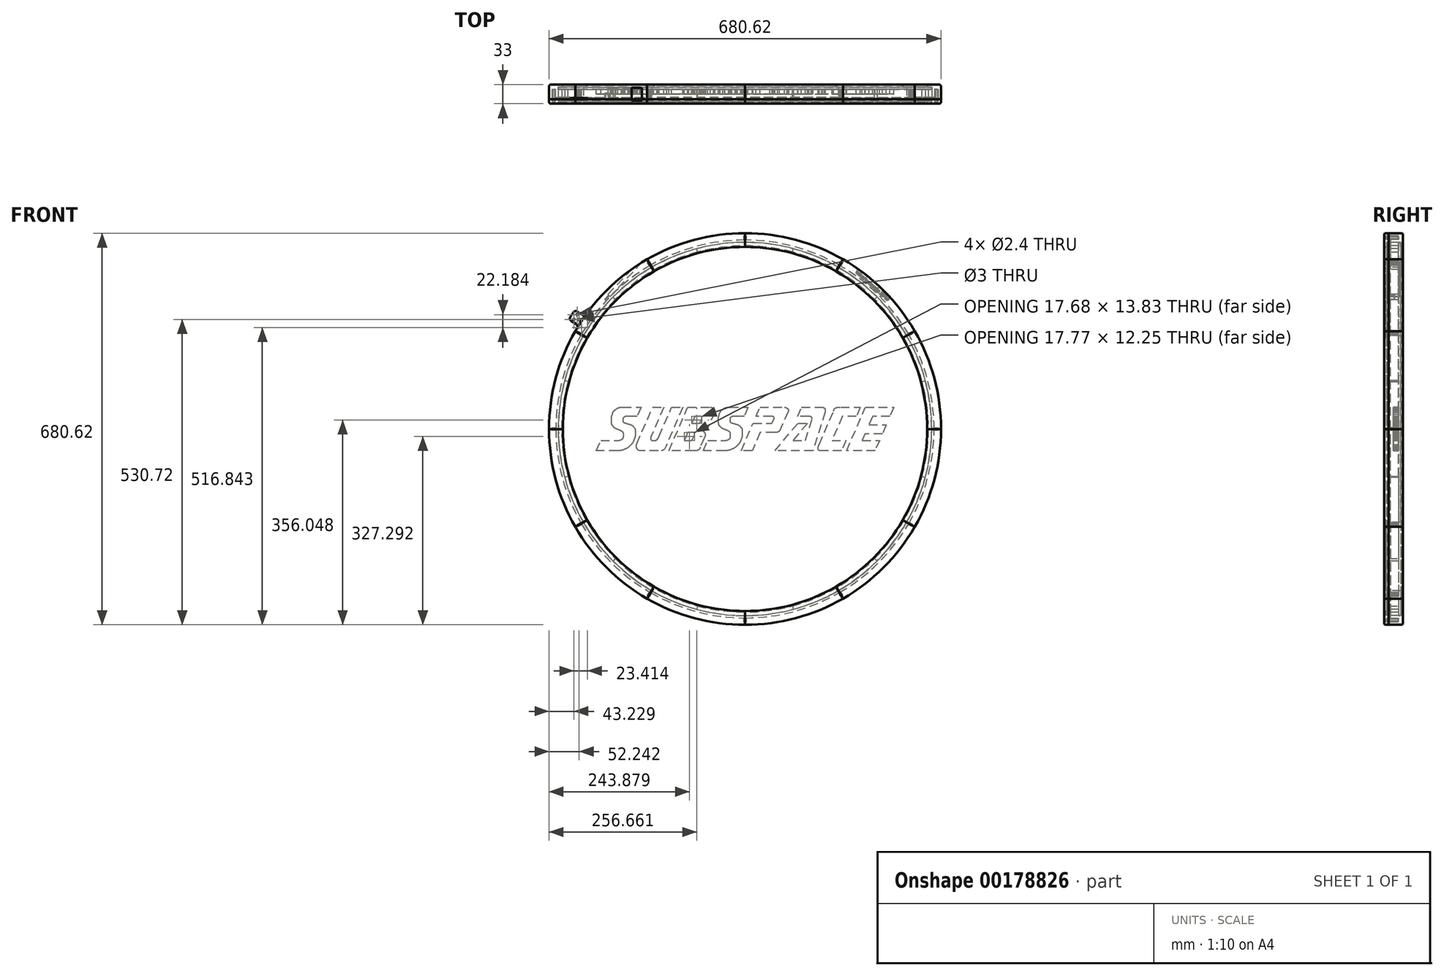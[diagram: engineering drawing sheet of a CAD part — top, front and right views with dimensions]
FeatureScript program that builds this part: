
annotation { "Feature Type Name" : "Feature", "Feature Type Description" : "" }
export const myFeature = defineFeature(function(context is Context, id is Id, definition is map)
    precondition{}
    {
        {
            assignVariable(context, id + "F0", {"name" : "depth", "anyValue" : 17 * mm});
        }
        {
            assignVariable(context, id + "F1", {"name" : "glassdepth", "anyValue" : 4 * mm});
        }
        {
            var Q0;
            Q0=qCreatedBy(makeId("Top.planeOp"),FACE);
            var sketch = newSketch(context, id + "F2", { "sketchPlane" : qUnion([Q0])});
            skLineSegment(sketch, "E0.bottom", {"start": v(0, 0) * mm, "end": v(-324.3, 0) * mm});
            skLineSegment(sketch, "E0.top", {"start": v(0, 4) * mm, "end": v(-324.3, 4) * mm});
            skLineSegment(sketch, "E0.left", {"start": v(0, 0) * mm, "end": v(0, 4) * mm});
            skLineSegment(sketch, "E0.right", {"start": v(-324.3, 0) * mm, "end": v(-324.3, 4) * mm});
            skLineSegment(sketch, "E1", {"start": v(-316.3, 8) * mm, "end": v(-340.3, 8) * mm});
            skLineSegment(sketch, "E2", {"start": v(-340.3, 8) * mm, "end": v(-340.3, -17) * mm});
            skLineSegment(sketch, "E3", {"start": v(-340.3, -17) * mm, "end": v(-324.3, -17) * mm});
            skLineSegment(sketch, "E4", {"start": v(-318.3, -17) * mm, "end": v(-318.3, 0) * mm});
            skLineSegment(sketch, "E5", {"start": v(-324.3, 0) * mm, "end": v(-324.3, 0) * mm});
            skLineSegment(sketch, "E6", {"start": v(-324.3, 0) * mm, "end": v(-324.3, -17) * mm});
            skLineSegment(sketch, "E7", {"start": v(-324.3, -17) * mm, "end": v(-324.3, -17) * mm});
            skLineSegment(sketch, "E8", {"start": v(-324.3, -17) * mm, "end": v(-318.3, -17) * mm});
            skLineSegment(sketch, "E9", {"start": v(-324.3, 4) * mm, "end": v(-316.3, 4) * mm});
            skLineSegment(sketch, "E10", {"start": v(-316.3, 4) * mm, "end": v(-316.3, 8) * mm});
            skLineSegment(sketch, "E11", {"start": v(0, 0) * mm, "end": v(0, -44.17) * mm, "construction": true});
            skLineSegment(sketch, "E12", {"start": v(-318.3, -8.5) * mm, "end": v(-340.3, -8.5) * mm, "construction": true});
            skLineSegment(sketch, "E13.MirrorCS", {"start": v(-324.3, -17) * mm, "end": v(-324.3, -21) * mm});
            skLineSegment(sketch, "E14.MirrorCS", {"start": v(-324.3, -21) * mm, "end": v(-316.3, -21) * mm});
            skLineSegment(sketch, "E15.MirrorCS", {"start": v(-316.3, -21) * mm, "end": v(-316.3, -25) * mm});
            skLineSegment(sketch, "E16.MirrorCS", {"start": v(-316.3, -25) * mm, "end": v(-340.3, -25) * mm});
            skLineSegment(sketch, "E17", {"start": v(-340.3, -25) * mm, "end": v(-340.3, -17) * mm});
            skSolve(sketch);
        }
        {
            var Q0;
            Q0=makeQuery(id+"F2.imprint","IMPRINT",FACE,{"disambiguationData":[TD([[makeQuery(id+"F2.imprint","IMPRINT",EDGE,{"derivedFrom":sQuery(id+"F2.wireOp",EDGE,"E4")}),1.0]])]});
            var Q1;
            Q1=sQuery(id+"F2.wireOp",EDGE,"E11");
            revolve(context, id + "F3", {"entities" : qUnion([Q0]), "axis" : qUnion([Q1]), "revolveType" : RevolveType.ONE_DIRECTION, "oppositeDirection" : true, "angle" : 30 * degree});
        }
        {
            var Q0;
            Q0=makeQuery(id+"F2.imprint","IMPRINT",FACE,{"disambiguationData":[TD([[makeQuery(id+"F2.imprint","IMPRINT",EDGE,{"derivedFrom":sQuery(id+"F2.wireOp",EDGE,"E0.right")}),1.0]])]});
            var Q1;
            Q1=sQuery(id+"F2.wireOp",EDGE,"E11");
            revolve(context, id + "F4", {"entities" : qUnion([Q0]), "axis" : qUnion([Q1]), "revolveType" : RevolveType.ONE_DIRECTION, "oppositeDirection" : true, "angle" : 30 * degree});
        }
        {
            var Q0;
            Q0=makeQuery(id+"F2.imprint","IMPRINT",FACE,{"disambiguationData":[TD([[makeQuery(id+"F2.imprint","IMPRINT",EDGE,{"derivedFrom":sQuery(id+"F2.wireOp",EDGE,"E3")}),-1.0]])]});
            var Q1;
            Q1=sQuery(id+"F2.wireOp",EDGE,"E11");
            revolve(context, id + "F5", {"entities" : qUnion([Q0]), "axis" : qUnion([Q1]), "revolveType" : RevolveType.ONE_DIRECTION, "oppositeDirection" : true, "angle" : 30 * degree});
        }
        {
            var Q0;
            Q0=makeQuery(id+"F4.opRevolve","SWEPT_EDGE",EDGE,{"disambiguationData":[OSD([sQuery(id+"F2.wireOp",EDGE,"E1"),sQuery(id+"F2.wireOp",EDGE,"E10")])]});
            var Q1;
            Q1=makeQuery(id+"F4.opRevolve","SWEPT_EDGE",EDGE,{"disambiguationData":[OSD([sQuery(id+"F2.wireOp",EDGE,"E1"),sQuery(id+"F2.wireOp",EDGE,"E2")])]});
            var Q2;
            Q2=makeQuery(id+"F5.opRevolve","SWEPT_EDGE",EDGE,{"disambiguationData":[OSD([sQuery(id+"F2.wireOp",EDGE,"E16.MirrorCS"),sQuery(id+"F2.wireOp",EDGE,"E17")])]});
            var Q3;
            Q3=makeQuery(id+"F5.opRevolve","SWEPT_EDGE",EDGE,{"disambiguationData":[OSD([sQuery(id+"F2.wireOp",EDGE,"E15.MirrorCS"),sQuery(id+"F2.wireOp",EDGE,"E16.MirrorCS")])]});
            fillet(context, id + "F6", {"entities" : qUnion([Q0, Q1, Q2, Q3]), "radius" : 3 * mm, "tangentPropagation" : true, "allowEdgeOverflow" : false});
        }
        {
            var Q0;
            Q0=makeQuery(id+"F2.imprint","IMPRINT",FACE,{"disambiguationData":[TD([[makeQuery(id+"F2.imprint","IMPRINT",EDGE,{"derivedFrom":sQuery(id+"F2.wireOp",EDGE,"E0.top")}),1.0]])]});
            var Q1;
            Q1=sQuery(id+"F2.wireOp",EDGE,"E11");
            revolve(context, id + "F7", {"entities" : qUnion([Q0]), "axis" : qUnion([Q1]), "revolveType" : RevolveType.FULL});
        }
        {
            var Q0;
            Q0=makeQuery(id+"F4.opRevolve","SWEPT_FACE",FACE,{"disambiguationData":[OSD([sQuery(id+"F2.wireOp",EDGE,"E3")])]});
            var sketch = newSketch(context, id + "F8", { "sketchPlane" : qUnion([Q0])});
            skLineSegment(sketch, "E18", {"start": v(-332.3, 0) * mm, "end": v(-333.8, 0) * mm});
            skLineSegment(sketch, "E19", {"start": v(-333.8, 0) * mm, "end": v(-335.3, 2) * mm});
            skLineSegment(sketch, "E20", {"start": v(-335.3, 2) * mm, "end": v(-332.3, 2) * mm});
            skLineSegment(sketch, "E21", {"start": v(-332.3, 2) * mm, "end": v(-332.3, 0) * mm, "construction": true});
            skLineSegment(sketch, "E22.MirrorCS", {"start": v(-329.3, 2) * mm, "end": v(-332.3, 2) * mm});
            skLineSegment(sketch, "E23.MirrorCS", {"start": v(-330.8, 0) * mm, "end": v(-329.3, 2) * mm});
            skLineSegment(sketch, "E24.MirrorCS", {"start": v(-332.3, 0) * mm, "end": v(-330.8, 0) * mm});
            skLineSegment(sketch, "E25.MirrorCS", {"start": v(-330.8, 0) * mm, "end": v(-329.3, -2) * mm});
            skLineSegment(sketch, "E26.MirrorCS", {"start": v(-329.3, -2) * mm, "end": v(-332.3, -2) * mm});
            skLineSegment(sketch, "E27.MirrorCS", {"start": v(-335.3, -2) * mm, "end": v(-332.3, -2) * mm});
            skLineSegment(sketch, "E28.MirrorCS", {"start": v(-333.8, 0) * mm, "end": v(-335.3, -2) * mm});
            skSolve(sketch);
        }
        {
            var Q0;
            Q0=makeQuery(id+"F8.imprint","IMPRINT",FACE,{"disambiguationData":[TD([[makeQuery(id+"F8.imprint","IMPRINT",EDGE,{"derivedFrom":sQuery(id+"F8.wireOp",EDGE,"E18")}),1.0]])]});
            extrude(context, id + "F9", {"entities" : qUnion([Q0]), "operationType" : NewBodyOperationType.REMOVE, "oppositeDirection" : true, "depth" : getVariable(context, 'depth'), "hasSecondDirection" : true, "secondDirectionOppositeDirection" : false, "secondDirectionDepth" : getVariable(context, 'glassdepth')});
        }
        {
            var Q0;
            Q0=makeQuery(id+"F8.imprint","IMPRINT",FACE,{"disambiguationData":[TD([[makeQuery(id+"F8.imprint","IMPRINT",EDGE,{"derivedFrom":sQuery(id+"F8.wireOp",EDGE,"E18")}),-1.0]])]});
            var Q1;
            Q1=makeQuery(id+"F8.imprint","IMPRINT",FACE,{"disambiguationData":[TD([[makeQuery(id+"F8.imprint","IMPRINT",EDGE,{"derivedFrom":sQuery(id+"F8.wireOp",EDGE,"E18")}),1.0]])]});
            var Q2;
            Q2=makeQuery(id+"F9.boolean.opBoolean","COPY",FACE,{"derivedFrom":makeQuery(id+"F9.opExtrude","CAP_FACE",FACE,{"disambiguationData":[OSD([sQuery(id+"F8.wireOp",EDGE,"E18"),sQuery(id+"F8.wireOp",EDGE,"E19"),sQuery(id+"F8.wireOp",EDGE,"E20"),sQuery(id+"F8.wireOp",EDGE,"E22.MirrorCS"),sQuery(id+"F8.wireOp",EDGE,"E23.MirrorCS"),sQuery(id+"F8.wireOp",EDGE,"E24.MirrorCS")])],"isStart":false})});
            var Q3;
            Q3=makeQuery(id+"F9.boolean.opBoolean","COPY",FACE,{"derivedFrom":makeQuery(id+"F9.opExtrude","CAP_FACE",FACE,{"disambiguationData":[OSD([sQuery(id+"F8.wireOp",EDGE,"E18"),sQuery(id+"F8.wireOp",EDGE,"E19"),sQuery(id+"F8.wireOp",EDGE,"E20"),sQuery(id+"F8.wireOp",EDGE,"E22.MirrorCS"),sQuery(id+"F8.wireOp",EDGE,"E23.MirrorCS"),sQuery(id+"F8.wireOp",EDGE,"E24.MirrorCS")])],"isStart":true})});
            extrude(context, id + "F10", {"entities" : qUnion([Q0, Q1]), "endBound" : BoundingType.UP_TO_SURFACE, "oppositeDirection" : true, "endBoundEntityFace" : qUnion([Q2]), "depth" : 25 * mm, "hasSecondDirection" : true, "secondDirectionBound" : SecondDirectionBoundingType.UP_TO_SURFACE, "secondDirectionOppositeDirection" : false, "secondDirectionBoundEntityFace" : qUnion([Q3]), "secondDirectionDepth" : 25 * mm});
        }
        {
            var Q0;
            Q0=makeQuery(id+"F4.opRevolve","SWEPT_EDGE",EDGE,{"disambiguationData":[OSD([sQuery(id+"F2.wireOp",EDGE,"E2"),sQuery(id+"F2.wireOp",EDGE,"E3")])]});
            cPoint(context, id + "F11", {"entities" : qUnion([Q0]), "parameter" : 0.5});
        }
        {
            var Q0;
            {var subQ0=sQuery(id+"F2.wireOp",EDGE,"E2");Q0=makeQuery(id+"F6.opFillet","BLEND_EDGE",EDGE,{"blendedFrom":[makeQuery(id+"F4.opRevolve","SWEPT_EDGE",EDGE,{"disambiguationData":[OSD([sQuery(id+"F2.wireOp",EDGE,"E1"),subQ0])]}),makeQuery(id+"F4.opRevolve","SWEPT_FACE",FACE,{"disambiguationData":[OSD([subQ0])]})],"blendedInto":[makeQuery(id+"F4.opRevolve","SWEPT_FACE",FACE,{"disambiguationData":[OSD([subQ0])]})]});}
            cPoint(context, id + "F12", {"entities" : qUnion([Q0]), "parameter" : 0.5});
        }
        {
            var Q0;
            Q0=qCreatedBy(makeId("Origin.pointOp"),VERTEX);
            var Q1;
            Q1 = qCreatedBy(id + "F11" ,VERTEX);
            var Q2;
            Q2 = qCreatedBy(id + "F12" ,VERTEX);
            cPlane(context, id + "F13", {"entities" : qUnion([Q0, Q1, Q2]), "cplaneType" : CPlaneType.THREE_POINT, "offset" : 25 * mm, "width" : 150 * mm, "height" : 150 * mm});
        }
        {
            var Q0;
            Q0=makeQuery(id+"F4.opRevolve","CAP_FACE",FACE,{"disambiguationData":[OSD([sQuery(id+"F2.wireOp",EDGE,"E0.right"),sQuery(id+"F2.wireOp",EDGE,"E1"),sQuery(id+"F2.wireOp",EDGE,"E2"),sQuery(id+"F2.wireOp",EDGE,"E3"),sQuery(id+"F2.wireOp",EDGE,"E6"),sQuery(id+"F2.wireOp",EDGE,"E9"),sQuery(id+"F2.wireOp",EDGE,"E10")])],"isStart":true});
            var sketch = newSketch(context, id + "F14", { "sketchPlane" : qUnion([Q0])});
            skLineSegment(sketch, "E29.bottom", {"start": v(-324.3, 17) * mm, "end": v(-328.3, 17) * mm});
            skLineSegment(sketch, "E29.top", {"start": v(-324.3, 14) * mm, "end": v(-328.3, 14) * mm});
            skLineSegment(sketch, "E29.left", {"start": v(-324.3, 17) * mm, "end": v(-324.3, 14) * mm});
            skLineSegment(sketch, "E29.right", {"start": v(-328.3, 17) * mm, "end": v(-328.3, 14) * mm});
            skSolve(sketch);
        }
        {
            var Q0;
            Q0=makeQuery(id+"F14.imprint","IMPRINT",FACE,{"disambiguationData":[TD([[makeQuery(id+"F14.imprint","IMPRINT",EDGE,{"derivedFrom":sQuery(id+"F14.wireOp",EDGE,"E29.bottom")}),-1.0]])]});
            var Q1;
            Q1=sQuery(id+"F2.wireOp",EDGE,"E11");
            revolve(context, id + "F15", {"operationType" : NewBodyOperationType.REMOVE, "entities" : qUnion([Q0]), "axis" : qUnion([Q1]), "revolveType" : RevolveType.FULL, "oppositeDirection" : true});
        }
        {
            var Q0;
            Q0=makeQuery(id+"F3.opRevolve","SWEPT_BODY",BODY,{"disambiguationData":[OSD([sQuery(id+"F2.wireOp",EDGE,"E0.bottom"),sQuery(id+"F2.wireOp",EDGE,"E4"),sQuery(id+"F2.wireOp",EDGE,"E5"),sQuery(id+"F2.wireOp",EDGE,"E6"),sQuery(id+"F2.wireOp",EDGE,"E8")])]});
            var Q1;
            Q1=sQuery(id+"F2.wireOp",EDGE,"E11");
            transform(context, id + "F16", {"entities" : qUnion([Q0]), "transformType" : TransformType.ROTATION, "transformAxis" : qUnion([Q1]), "angle" : 30 * degree / 2, "oppositeDirection" : true, "makeCopy" : false});
        }
        {
            var Q0;
            Q0=makeQuery(id+"F3.opRevolve","SWEPT_BODY",BODY,{"disambiguationData":[OSD([sQuery(id+"F2.wireOp",EDGE,"E0.bottom"),sQuery(id+"F2.wireOp",EDGE,"E4"),sQuery(id+"F2.wireOp",EDGE,"Gf9DX7O2-zRGB-o6pw-WBMw-vOaWXiKhR38r"),sQuery(id+"F2.wireOp",EDGE,"UBI3kVvU-87iV-WFw2-skFk-959g78KHDnDF"),sQuery(id+"F2.wireOp",EDGE,"vs7l4pqw-Zqkt-XyLA-M46B-TnmlfDFsNGoH"),sQuery(id+"F2.wireOp",EDGE,"IAT4wlYG-pcC1-2uCw-kGJ2-k2milrRGhkYf"),sQuery(id+"F2.wireOp",EDGE,"E5"),sQuery(id+"F2.wireOp",EDGE,"E6"),sQuery(id+"F2.wireOp",EDGE,"E8")])]});
            var Q1;
            Q1=makeQuery(id+"F4.opRevolve","SWEPT_BODY",BODY,{"disambiguationData":[OSD([sQuery(id+"F2.wireOp",EDGE,"E0.right"),sQuery(id+"F2.wireOp",EDGE,"E1"),sQuery(id+"F2.wireOp",EDGE,"E2"),sQuery(id+"F2.wireOp",EDGE,"E3"),sQuery(id+"F2.wireOp",EDGE,"E5"),sQuery(id+"F2.wireOp",EDGE,"E6"),sQuery(id+"F2.wireOp",EDGE,"E9"),sQuery(id+"F2.wireOp",EDGE,"E10")])]});
            var Q2;
            Q2=makeQuery(id+"F5.opRevolve","SWEPT_BODY",BODY,{"disambiguationData":[OSD([sQuery(id+"F2.wireOp",EDGE,"E3"),sQuery(id+"F2.wireOp",EDGE,"E13.MirrorCS"),sQuery(id+"F2.wireOp",EDGE,"E14.MirrorCS"),sQuery(id+"F2.wireOp",EDGE,"E15.MirrorCS"),sQuery(id+"F2.wireOp",EDGE,"E16.MirrorCS"),sQuery(id+"F2.wireOp",EDGE,"E17")])]});
            var Q3;
            Q3=makeQuery(id+"F10.opExtrude","SWEPT_BODY",BODY,{"disambiguationData":[OSD([sQuery(id+"F8.wireOp",EDGE,"E19"),sQuery(id+"F8.wireOp",EDGE,"E20"),sQuery(id+"F8.wireOp",EDGE,"E22.MirrorCS"),sQuery(id+"F8.wireOp",EDGE,"E23.MirrorCS"),sQuery(id+"F8.wireOp",EDGE,"E25.MirrorCS"),sQuery(id+"F8.wireOp",EDGE,"E26.MirrorCS"),sQuery(id+"F8.wireOp",EDGE,"E27.MirrorCS"),sQuery(id+"F8.wireOp",EDGE,"E28.MirrorCS")])]});
            var Q4;
            Q4=sQuery(id+"F2.wireOp",EDGE,"E11");
            circularPattern(context, id + "F17", {"entities" : qUnion([Q0, Q1, Q2, Q3]), "axis" : qUnion([Q4]), "angle" : 30 * degree, "instanceCount" : 12, "oppositeDirection" : true});
        }
        {
            var Q0;
            Q0=qCreatedBy(makeId("Front.planeOp"),FACE);
            var Q1;
            Q1=qCreatedBy(makeId("Front.planeOp"),FACE);
            var Q2;
            Q2=qCreatedBy(makeId("Front.planeOp"),FACE);
            var sketch = newSketch(context, id + "F18", { "sketchPlane" : qUnion([Q0, Q1, Q2])});
            skFitSpline(sketch, "E30", {"points": [v(-224.63, -19.84) * mm, v(-220.04, -19.84) * mm, v(-216.63, -19.23) * mm, v(-214.42, -18) * mm]});
            skFitSpline(sketch, "E31", {"points": [v(-214.42, -18) * mm, v(-212.2, -16.77) * mm, v(-211.1, -14.24) * mm, v(-211.1, -10.43) * mm]});
            skFitSpline(sketch, "E32", {"points": [v(-211.1, -10.43) * mm, v(-211.1, -7.6) * mm, v(-211.85, -5.65) * mm, v(-213.37, -4.58) * mm]});
            skFitSpline(sketch, "E33", {"points": [v(-213.37, -4.58) * mm, v(-214.89, -3.48) * mm, v(-217.43, -2.23) * mm, v(-221, -0.83) * mm]});
            skFitSpline(sketch, "E34", {"points": [v(-221, -0.83) * mm, v(-224.53, 0.56) * mm, v(-227.2, 2.33) * mm, v(-229, 4.46) * mm]});
            skFitSpline(sketch, "E35", {"points": [v(-229, 4.46) * mm, v(-230.8, 6.6) * mm, v(-231.77, 9.96) * mm, v(-231.9, 14.55) * mm]});
            skFitSpline(sketch, "E36", {"points": [v(-231.9, 14.55) * mm, v(-231.9, 18.73) * mm, v(-231.34, 22.5) * mm, v(-230.23, 25.87) * mm]});
            skFitSpline(sketch, "E37", {"points": [v(-230.23, 25.87) * mm, v(-229.12, 29.24) * mm, v(-227.13, 32) * mm, v(-224.26, 34.18) * mm]});
            skFitSpline(sketch, "E38", {"points": [v(-224.26, 34.18) * mm, v(-221.4, 36.4) * mm, v(-217.43, 37.5) * mm, v(-212.39, 37.5) * mm]});
            skLineSegment(sketch, "E39", {"start": v(-258.35, -37.5) * mm, "end": v(-250.41, -19.84) * mm});
            skLineSegment(sketch, "E40", {"start": v(-250.41, -19.84) * mm, "end": v(-224.63, -19.84) * mm});
            skFitSpline(sketch, "E41", {"points": [v(-203.16, 21.75) * mm, v(-206.48, 21.75) * mm, v(-208.8, 21.3) * mm, v(-210.11, 20.4) * mm]});
            skFitSpline(sketch, "E42", {"points": [v(-210.11, 20.4) * mm, v(-211.38, 19.5) * mm, v(-212.02, 17.75) * mm, v(-212.02, 15.17) * mm]});
            skFitSpline(sketch, "E43", {"points": [v(-212.02, 15.17) * mm, v(-212.02, 13.03) * mm, v(-210.79, 11.52) * mm, v(-208.33, 10.61) * mm]});
            skFitSpline(sketch, "E44", {"points": [v(-208.33, 10.61) * mm, v(-205.87, 9.75) * mm, v(-203.26, 8.91) * mm, v(-200.51, 8.1) * mm]});
            skFitSpline(sketch, "E45", {"points": [v(-200.51, 8.1) * mm, v(-197.76, 7.27) * mm, v(-195.43, 5.73) * mm, v(-193.5, 3.48) * mm]});
            skFitSpline(sketch, "E46", {"points": [v(-193.5, 3.48) * mm, v(-191.57, 1.22) * mm, v(-190.6, -2.35) * mm, v(-190.6, -7.23) * mm]});
            skFitSpline(sketch, "E47", {"points": [v(-190.6, -7.23) * mm, v(-190.6, -11.2) * mm, v(-191.32, -15.02) * mm, v(-192.76, -18.67) * mm]});
            skFitSpline(sketch, "E48", {"points": [v(-192.76, -18.67) * mm, v(-194.2, -22.32) * mm, v(-196.27, -25.56) * mm, v(-198.97, -28.4) * mm]});
            skFitSpline(sketch, "E49", {"points": [v(-198.97, -28.4) * mm, v(-201.68, -31.22) * mm, v(-204.96, -33.46) * mm, v(-208.82, -35.1) * mm]});
            skFitSpline(sketch, "E50", {"points": [v(-208.82, -35.1) * mm, v(-212.63, -36.7) * mm, v(-216.76, -37.5) * mm, v(-221.19, -37.5) * mm]});
            skLineSegment(sketch, "E51", {"start": v(-212.39, 37.5) * mm, "end": v(-180.52, 37.5) * mm});
            skLineSegment(sketch, "E52", {"start": v(-180.52, 37.5) * mm, "end": v(-187.28, 21.75) * mm});
            skLineSegment(sketch, "E53", {"start": v(-187.28, 21.75) * mm, "end": v(-203.16, 21.75) * mm});
            skLineSegment(sketch, "E54", {"start": v(-221.19, -37.5) * mm, "end": v(-258.35, -37.5) * mm});
            skLineSegment(sketch, "E55", {"start": v(-258.35, -37.5) * mm, "end": v(-221.19, -37.5) * mm});
            skFitSpline(sketch, "E56", {"points": [v(-136.1, -26.8) * mm, v(-139.25, -33.93) * mm, v(-144.05, -37.5) * mm, v(-150.5, -37.5) * mm]});
            skLineSegment(sketch, "E57", {"start": v(-127.42, 37.5) * mm, "end": v(-108.16, 37.5) * mm});
            skLineSegment(sketch, "E58", {"start": v(-108.16, 37.5) * mm, "end": v(-136.1, -26.8) * mm});
            skFitSpline(sketch, "E59", {"points": [v(-182.98, -37.5) * mm, v(-184.13, -37.5) * mm, v(-185.36, -36.68) * mm, v(-186.67, -35.04) * mm]});
            skFitSpline(sketch, "E60", {"points": [v(-186.67, -35.04) * mm, v(-187.98, -33.36) * mm, v(-188.64, -31.45) * mm, v(-188.64, -29.32) * mm]});
            skFitSpline(sketch, "E61", {"points": [v(-188.64, -29.32) * mm, v(-188.64, -28.2) * mm, v(-188.4, -27.04) * mm, v(-187.9, -25.81) * mm]});
            skLineSegment(sketch, "E62", {"start": v(-150.5, -37.5) * mm, "end": v(-182.98, -37.5) * mm});
            skLineSegment(sketch, "E63", {"start": v(-182.98, -37.5) * mm, "end": v(-150.5, -37.5) * mm});
            skFitSpline(sketch, "E64", {"points": [v(-162.92, -12.7) * mm, v(-163.54, -14.06) * mm, v(-163.84, -15.27) * mm, v(-163.84, -16.34) * mm]});
            skFitSpline(sketch, "E65", {"points": [v(-163.84, -16.34) * mm, v(-163.84, -17.57) * mm, v(-163.47, -18.47) * mm, v(-162.74, -19.04) * mm]});
            skFitSpline(sketch, "E66", {"points": [v(-162.74, -19.04) * mm, v(-162, -19.58) * mm, v(-161.28, -19.84) * mm, v(-160.58, -19.84) * mm]});
            skLineSegment(sketch, "E67", {"start": v(-187.9, -25.81) * mm, "end": v(-160.46, 37.5) * mm});
            skLineSegment(sketch, "E68", {"start": v(-160.46, 37.5) * mm, "end": v(-141.14, 37.5) * mm});
            skLineSegment(sketch, "E69", {"start": v(-141.14, 37.5) * mm, "end": v(-162.92, -12.7) * mm});
            skFitSpline(sketch, "E70", {"points": [v(-158.43, -19.84) * mm, v(-155.97, -19.84) * mm, v(-154.12, -19.33) * mm, v(-152.9, -18.3) * mm]});
            skFitSpline(sketch, "E71", {"points": [v(-152.9, -18.3) * mm, v(-151.66, -17.24) * mm, v(-150.43, -15.3) * mm, v(-149.2, -12.52) * mm]});
            skLineSegment(sketch, "E72", {"start": v(-160.58, -19.84) * mm, "end": v(-158.43, -19.84) * mm});
            skLineSegment(sketch, "E73", {"start": v(-158.43, -19.84) * mm, "end": v(-160.58, -19.84) * mm});
            skLineSegment(sketch, "E74", {"start": v(-149.2, -12.52) * mm, "end": v(-127.42, 37.5) * mm});
            skLineSegment(sketch, "E75", {"start": v(-127.42, 37.5) * mm, "end": v(-149.2, -12.52) * mm});
            skFitSpline(sketch, "E76", {"points": [v(-60.3, 37.5) * mm, v(-58.2, 37.5) * mm, v(-56.38, 36.82) * mm, v(-54.82, 35.47) * mm]});
            skFitSpline(sketch, "E77", {"points": [v(-54.82, 35.47) * mm, v(-53.26, 34.12) * mm, v(-52.48, 32.56) * mm, v(-52.48, 30.8) * mm]});
            skFitSpline(sketch, "E78", {"points": [v(-52.48, 30.8) * mm, v(-52.48, 30.3) * mm, v(-52.6, 29.7) * mm, v(-52.85, 29) * mm]});
            skLineSegment(sketch, "E79", {"start": v(-89.03, -37.5) * mm, "end": v(-132.22, -37.5) * mm});
            skLineSegment(sketch, "E80", {"start": v(-132.22, -37.5) * mm, "end": v(-99.61, 37.5) * mm});
            skLineSegment(sketch, "E81", {"start": v(-99.61, 37.5) * mm, "end": v(-60.3, 37.5) * mm});
            skFitSpline(sketch, "E82", {"points": [v(-64.66, 1.57) * mm, v(-65.36, -0.11) * mm, v(-66.43, -1.18) * mm, v(-67.86, -1.63) * mm]});
            skFitSpline(sketch, "E83", {"points": [v(-67.86, -1.63) * mm, v(-69.26, -2.04) * mm, v(-71.27, -2.25) * mm, v(-73.9, -2.25) * mm]});
            skFitSpline(sketch, "E84", {"points": [v(-73.9, -2.25) * mm, v(-72.5, -3.48) * mm, v(-71.4, -4.7) * mm, v(-70.57, -5.94) * mm]});
            skFitSpline(sketch, "E85", {"points": [v(-70.57, -5.94) * mm, v(-69.75, -7.17) * mm, v(-69.34, -8.62) * mm, v(-69.34, -10.3) * mm]});
            skFitSpline(sketch, "E86", {"points": [v(-69.34, -10.3) * mm, v(-69.34, -11.78) * mm, v(-69.73, -13.36) * mm, v(-70.5, -15.04) * mm]});
            skLineSegment(sketch, "E87", {"start": v(-52.85, 29) * mm, "end": v(-64.66, 1.57) * mm});
            skLineSegment(sketch, "E88", {"start": v(-64.66, 1.57) * mm, "end": v(-52.85, 29) * mm});
            skFitSpline(sketch, "E89", {"points": [v(-77.65, -31.47) * mm, v(-79.5, -35.5) * mm, v(-83.29, -37.5) * mm, v(-89.03, -37.5) * mm]});
            skLineSegment(sketch, "E90", {"start": v(-70.5, -15.04) * mm, "end": v(-77.65, -31.47) * mm});
            skLineSegment(sketch, "E91", {"start": v(-77.65, -31.47) * mm, "end": v(-70.5, -15.04) * mm});
            skFitSpline(sketch, "E92", {"points": [v(-97.46, -19.84) * mm, v(-93.8, -19.84) * mm, v(-91.49, -18.84) * mm, v(-90.5, -16.83) * mm]});
            skLineSegment(sketch, "E93", {"start": v(-105.27, -19.84) * mm, "end": v(-97.46, -19.84) * mm});
            skLineSegment(sketch, "E94", {"start": v(-97.46, -19.84) * mm, "end": v(-105.27, -19.84) * mm});
            skFitSpline(sketch, "E95", {"points": [v(-88.1, -11.66) * mm, v(-87.78, -10.88) * mm, v(-87.61, -10.08) * mm, v(-87.61, -9.26) * mm]});
            skFitSpline(sketch, "E96", {"points": [v(-87.61, -9.26) * mm, v(-87.61, -8.36) * mm, v(-87.88, -7.62) * mm, v(-88.41, -7.04) * mm]});
            skFitSpline(sketch, "E97", {"points": [v(-88.41, -7.04) * mm, v(-88.95, -6.43) * mm, v(-89.56, -6.12) * mm, v(-90.26, -6.12) * mm]});
            skLineSegment(sketch, "E98", {"start": v(-90.5, -16.83) * mm, "end": v(-88.1, -11.66) * mm});
            skLineSegment(sketch, "E99", {"start": v(-88.1, -11.66) * mm, "end": v(-90.5, -16.83) * mm});
            skLineSegment(sketch, "E100", {"start": v(-90.26, -6.12) * mm, "end": v(-99.36, -6.12) * mm});
            skLineSegment(sketch, "E101", {"start": v(-99.36, -6.12) * mm, "end": v(-105.27, -19.84) * mm});
            skFitSpline(sketch, "E102", {"points": [v(-83.98, 9.63) * mm, v(-81.97, 9.63) * mm, v(-80.46, 9.83) * mm, v(-79.43, 10.24) * mm]});
            skFitSpline(sketch, "E103", {"points": [v(-79.43, 10.24) * mm, v(-78.36, 10.65) * mm, v(-77.56, 11.54) * mm, v(-77.03, 12.89) * mm]});
            skLineSegment(sketch, "E104", {"start": v(-87.12, 21.75) * mm, "end": v(-92.53, 9.63) * mm});
            skLineSegment(sketch, "E105", {"start": v(-92.53, 9.63) * mm, "end": v(-83.98, 9.63) * mm});
            skFitSpline(sketch, "E106", {"points": [v(-74.88, 18.55) * mm, v(-74.88, 20.68) * mm, v(-76.1, 21.75) * mm, v(-78.57, 21.75) * mm]});
            skLineSegment(sketch, "E107", {"start": v(-77.03, 12.89) * mm, "end": v(-74.88, 18.55) * mm});
            skLineSegment(sketch, "E108", {"start": v(-74.88, 18.55) * mm, "end": v(-77.03, 12.89) * mm});
            skLineSegment(sketch, "E109", {"start": v(-78.57, 21.75) * mm, "end": v(-87.12, 21.75) * mm});
            skLineSegment(sketch, "E110", {"start": v(-87.12, 21.75) * mm, "end": v(-78.57, 21.75) * mm});
            skFitSpline(sketch, "E111", {"points": [v(-38.82, -19.84) * mm, v(-34.23, -19.84) * mm, v(-30.82, -19.23) * mm, v(-28.6, -18) * mm]});
            skFitSpline(sketch, "E112", {"points": [v(-28.6, -18) * mm, v(-26.4, -16.77) * mm, v(-25.29, -14.24) * mm, v(-25.29, -10.43) * mm]});
            skFitSpline(sketch, "E113", {"points": [v(-25.29, -10.43) * mm, v(-25.29, -7.6) * mm, v(-26.05, -5.65) * mm, v(-27.56, -4.58) * mm]});
            skFitSpline(sketch, "E114", {"points": [v(-27.56, -4.58) * mm, v(-29.08, -3.48) * mm, v(-31.62, -2.23) * mm, v(-35.2, -0.83) * mm]});
            skFitSpline(sketch, "E115", {"points": [v(-35.2, -0.83) * mm, v(-38.72, 0.56) * mm, v(-41.39, 2.33) * mm, v(-43.2, 4.46) * mm]});
            skFitSpline(sketch, "E116", {"points": [v(-43.2, 4.46) * mm, v(-45, 6.6) * mm, v(-45.96, 9.96) * mm, v(-46.08, 14.55) * mm]});
            skFitSpline(sketch, "E117", {"points": [v(-46.08, 14.55) * mm, v(-46.08, 18.73) * mm, v(-45.53, 22.5) * mm, v(-44.42, 25.87) * mm]});
            skFitSpline(sketch, "E118", {"points": [v(-44.42, 25.87) * mm, v(-43.31, 29.24) * mm, v(-41.32, 32) * mm, v(-38.45, 34.18) * mm]});
            skFitSpline(sketch, "E119", {"points": [v(-38.45, 34.18) * mm, v(-35.58, 36.4) * mm, v(-31.62, 37.5) * mm, v(-26.58, 37.5) * mm]});
            skLineSegment(sketch, "E120", {"start": v(-72.54, -37.5) * mm, "end": v(-64.6, -19.84) * mm});
            skLineSegment(sketch, "E121", {"start": v(-64.6, -19.84) * mm, "end": v(-38.82, -19.84) * mm});
            skFitSpline(sketch, "E122", {"points": [v(-17.35, 21.75) * mm, v(-20.67, 21.75) * mm, v(-23, 21.3) * mm, v(-24.3, 20.4) * mm]});
            skFitSpline(sketch, "E123", {"points": [v(-24.3, 20.4) * mm, v(-25.57, 19.5) * mm, v(-26.21, 17.75) * mm, v(-26.21, 15.17) * mm]});
            skFitSpline(sketch, "E124", {"points": [v(-26.21, 15.17) * mm, v(-26.21, 13.03) * mm, v(-24.98, 11.52) * mm, v(-22.52, 10.61) * mm]});
            skFitSpline(sketch, "E125", {"points": [v(-22.52, 10.61) * mm, v(-20.06, 9.75) * mm, v(-17.45, 8.91) * mm, v(-14.7, 8.1) * mm]});
            skFitSpline(sketch, "E126", {"points": [v(-14.7, 8.1) * mm, v(-11.96, 7.27) * mm, v(-9.62, 5.73) * mm, v(-7.7, 3.48) * mm]});
            skFitSpline(sketch, "E127", {"points": [v(-7.7, 3.48) * mm, v(-5.76, 1.22) * mm, v(-4.8, -2.35) * mm, v(-4.8, -7.23) * mm]});
            skFitSpline(sketch, "E128", {"points": [v(-4.8, -7.23) * mm, v(-4.8, -11.2) * mm, v(-5.52, -15.02) * mm, v(-6.95, -18.67) * mm]});
            skFitSpline(sketch, "E129", {"points": [v(-6.95, -18.67) * mm, v(-8.39, -22.32) * mm, v(-10.46, -25.56) * mm, v(-13.17, -28.4) * mm]});
            skFitSpline(sketch, "E130", {"points": [v(-13.17, -28.4) * mm, v(-15.87, -31.22) * mm, v(-19.16, -33.46) * mm, v(-23.01, -35.1) * mm]});
            skFitSpline(sketch, "E131", {"points": [v(-23.01, -35.1) * mm, v(-26.83, -36.7) * mm, v(-30.95, -37.5) * mm, v(-35.38, -37.5) * mm]});
            skLineSegment(sketch, "E132", {"start": v(-26.58, 37.5) * mm, "end": v(5.3, 37.5) * mm});
            skLineSegment(sketch, "E133", {"start": v(5.3, 37.5) * mm, "end": v(-1.48, 21.75) * mm});
            skLineSegment(sketch, "E134", {"start": v(-1.48, 21.75) * mm, "end": v(-17.35, 21.75) * mm});
            skLineSegment(sketch, "E135", {"start": v(-35.38, -37.5) * mm, "end": v(-72.54, -37.5) * mm});
            skLineSegment(sketch, "E136", {"start": v(-72.54, -37.5) * mm, "end": v(-35.38, -37.5) * mm});
            skFitSpline(sketch, "E137", {"points": [v(43.2, 9.75) * mm, v(45.53, 9.75) * mm, v(47.17, 10.8) * mm, v(48.11, 12.89) * mm]});
            skLineSegment(sketch, "E138", {"start": v(-6.58, -37.5) * mm, "end": v(13.97, 9.75) * mm});
            skLineSegment(sketch, "E139", {"start": v(13.97, 9.75) * mm, "end": v(43.2, 9.75) * mm});
            skFitSpline(sketch, "E140", {"points": [v(50.64, 18.55) * mm, v(50.64, 19.66) * mm, v(50.29, 20.46) * mm, v(49.59, 20.95) * mm]});
            skFitSpline(sketch, "E141", {"points": [v(49.59, 20.95) * mm, v(48.9, 21.48) * mm, v(48.01, 21.75) * mm, v(46.94, 21.75) * mm]});
            skLineSegment(sketch, "E142", {"start": v(48.11, 12.89) * mm, "end": v(50.64, 18.55) * mm});
            skLineSegment(sketch, "E143", {"start": v(50.64, 18.55) * mm, "end": v(48.11, 12.89) * mm});
            skFitSpline(sketch, "E144", {"points": [v(68.66, 37.5) * mm, v(70.39, 37.5) * mm, v(71.92, 36.93) * mm, v(73.28, 35.78) * mm]});
            skFitSpline(sketch, "E145", {"points": [v(73.28, 35.78) * mm, v(74.63, 34.63) * mm, v(75.3, 33.25) * mm, v(75.3, 31.66) * mm]});
            skFitSpline(sketch, "E146", {"points": [v(75.3, 31.66) * mm, v(75.3, 31.12) * mm, v(75.18, 30.55) * mm, v(74.94, 29.93) * mm]});
            skLineSegment(sketch, "E147", {"start": v(46.94, 21.75) * mm, "end": v(19.13, 21.75) * mm});
            skLineSegment(sketch, "E148", {"start": v(19.13, 21.75) * mm, "end": v(25.9, 37.5) * mm});
            skLineSegment(sketch, "E149", {"start": v(25.9, 37.5) * mm, "end": v(68.66, 37.5) * mm});
            skFitSpline(sketch, "E150", {"points": [v(62.2, 1.32) * mm, v(61.14, -0.97) * mm, v(60.3, -2.55) * mm, v(59.68, -3.41) * mm]});
            skFitSpline(sketch, "E151", {"points": [v(59.68, -3.41) * mm, v(59.06, -4.28) * mm, v(58.12, -4.93) * mm, v(56.85, -5.38) * mm]});
            skFitSpline(sketch, "E152", {"points": [v(56.85, -5.38) * mm, v(55.62, -5.8) * mm, v(53.67, -6) * mm, v(51, -6) * mm]});
            skLineSegment(sketch, "E153", {"start": v(74.94, 29.93) * mm, "end": v(62.2, 1.32) * mm});
            skLineSegment(sketch, "E154", {"start": v(62.2, 1.32) * mm, "end": v(74.94, 29.93) * mm});
            skLineSegment(sketch, "E155", {"start": v(51, -6) * mm, "end": v(26.27, -6) * mm});
            skLineSegment(sketch, "E156", {"start": v(26.27, -6) * mm, "end": v(12.67, -37.5) * mm});
            skLineSegment(sketch, "E157", {"start": v(12.67, -37.5) * mm, "end": v(-6.58, -37.5) * mm});
            skFitSpline(sketch, "E158", {"points": [v(116.47, 17.07) * mm, v(116.47, 18.76) * mm, v(115.94, 19.94) * mm, v(114.87, 20.64) * mm]});
            skFitSpline(sketch, "E159", {"points": [v(114.87, 20.64) * mm, v(113.8, 21.38) * mm, v(112.49, 21.75) * mm, v(110.93, 21.75) * mm]});
            skLineSegment(sketch, "E160", {"start": v(117.95, -37.5) * mm, "end": v(51.93, -37.5) * mm});
            skLineSegment(sketch, "E161", {"start": v(51.93, -37.5) * mm, "end": v(91.86, 9.75) * mm});
            skLineSegment(sketch, "E162", {"start": v(91.86, 9.75) * mm, "end": v(108.4, 9.75) * mm});
            skLineSegment(sketch, "E163", {"start": v(108.4, 9.75) * mm, "end": v(83.3, -19.84) * mm});
            skLineSegment(sketch, "E164", {"start": v(83.3, -19.84) * mm, "end": v(104.96, -19.84) * mm});
            skLineSegment(sketch, "E165", {"start": v(104.96, -19.84) * mm, "end": v(116.47, 17.07) * mm});
            skFitSpline(sketch, "E166", {"points": [v(134.5, 37.5) * mm, v(135.97, 37.5) * mm, v(137.14, 37) * mm, v(138, 36.02) * mm]});
            skFitSpline(sketch, "E167", {"points": [v(138, 36.02) * mm, v(138.9, 35.08) * mm, v(139.36, 33.8) * mm, v(139.36, 32.2) * mm]});
            skFitSpline(sketch, "E168", {"points": [v(139.36, 32.2) * mm, v(139.36, 31.18) * mm, v(139.2, 30.2) * mm, v(138.86, 29.26) * mm]});
            skLineSegment(sketch, "E169", {"start": v(110.93, 21.75) * mm, "end": v(91.24, 21.75) * mm});
            skLineSegment(sketch, "E170", {"start": v(91.24, 21.75) * mm, "end": v(98.07, 37.5) * mm});
            skLineSegment(sketch, "E171", {"start": v(98.07, 37.5) * mm, "end": v(134.5, 37.5) * mm});
            skLineSegment(sketch, "E172", {"start": v(138.86, 29.26) * mm, "end": v(117.95, -37.5) * mm});
            skLineSegment(sketch, "E173", {"start": v(117.95, -37.5) * mm, "end": v(138.86, 29.26) * mm});
            skFitSpline(sketch, "E174", {"points": [v(133.14, -37.5) * mm, v(129.29, -37.5) * mm, v(127.36, -35.86) * mm, v(127.36, -32.58) * mm]});
            skFitSpline(sketch, "E175", {"points": [v(127.36, -32.58) * mm, v(127.36, -30.98) * mm, v(127.8, -29.13) * mm, v(128.71, -27.04) * mm]});
            skLineSegment(sketch, "E176", {"start": v(200.14, 37.5) * mm, "end": v(193.38, 21.75) * mm});
            skLineSegment(sketch, "E177", {"start": v(193.38, 21.75) * mm, "end": v(169.07, 21.75) * mm});
            skLineSegment(sketch, "E178", {"start": v(169.07, 21.75) * mm, "end": v(151.05, -19.84) * mm});
            skLineSegment(sketch, "E179", {"start": v(151.05, -19.84) * mm, "end": v(175.35, -19.84) * mm});
            skLineSegment(sketch, "E180", {"start": v(175.35, -19.84) * mm, "end": v(167.78, -37.5) * mm});
            skLineSegment(sketch, "E181", {"start": v(167.78, -37.5) * mm, "end": v(133.14, -37.5) * mm});
            skFitSpline(sketch, "E182", {"points": [v(153.81, 30.92) * mm, v(155.58, 35.3) * mm, v(159.68, 37.5) * mm, v(166.12, 37.5) * mm]});
            skLineSegment(sketch, "E183", {"start": v(128.71, -27.04) * mm, "end": v(153.81, 30.92) * mm});
            skLineSegment(sketch, "E184", {"start": v(153.81, 30.92) * mm, "end": v(128.71, -27.04) * mm});
            skLineSegment(sketch, "E185", {"start": v(166.12, 37.5) * mm, "end": v(200.14, 37.5) * mm});
            skLineSegment(sketch, "E186", {"start": v(200.14, 37.5) * mm, "end": v(166.12, 37.5) * mm});
            skLineSegment(sketch, "E187", {"start": v(225.98, -37.5) * mm, "end": v(176.58, -37.5) * mm});
            skLineSegment(sketch, "E188", {"start": v(176.58, -37.5) * mm, "end": v(209, 37.5) * mm});
            skLineSegment(sketch, "E189", {"start": v(209, 37.5) * mm, "end": v(258.35, 37.5) * mm});
            skLineSegment(sketch, "E190", {"start": v(258.35, 37.5) * mm, "end": v(251.58, 21.75) * mm});
            skLineSegment(sketch, "E191", {"start": v(251.58, 21.75) * mm, "end": v(221.43, 21.75) * mm});
            skLineSegment(sketch, "E192", {"start": v(221.43, 21.75) * mm, "end": v(215.16, 7.23) * mm});
            skLineSegment(sketch, "E193", {"start": v(215.16, 7.23) * mm, "end": v(245.43, 7.23) * mm});
            skLineSegment(sketch, "E194", {"start": v(245.43, 7.23) * mm, "end": v(238.6, -8.52) * mm});
            skLineSegment(sketch, "E195", {"start": v(238.6, -8.52) * mm, "end": v(208.33, -8.52) * mm});
            skLineSegment(sketch, "E196", {"start": v(208.33, -8.52) * mm, "end": v(203.47, -19.84) * mm});
            skLineSegment(sketch, "E197", {"start": v(203.47, -19.84) * mm, "end": v(233.68, -19.84) * mm});
            skLineSegment(sketch, "E198", {"start": v(233.68, -19.84) * mm, "end": v(225.98, -37.5) * mm});
            skSolve(sketch);
        }
        {
            var Q0;
            Q0 = qSketchRegion(id + "F18", true);
            extrude(context, id + "F19", {"entities" : qUnion([Q0]), "depth" : getVariable(context, 'depth') / 2});
        }
        {
            var Q0;
            Q0=makeQuery(id+"F17.opPattern","COPY",EDGE,{"derivedFrom":makeQuery(id+"F3.opRevolve","CAP_EDGE",EDGE,{"disambiguationData":[OSD([sQuery(id+"F2.wireOp",EDGE,"E4")])],"isStart":false}),"instanceName":"10"});
            cPoint(context, id + "F20", {"entities" : qUnion([Q0]), "parameter" : 0.5});
        }
        {
            var Q0;
            Q0=qCreatedBy(makeId("Front.planeOp"),FACE);
            var Q1;
            Q1 = qCreatedBy(id + "F20" ,VERTEX);
            cPlane(context, id + "F21", {"entities" : qUnion([Q0, Q1]), "cplaneType" : CPlaneType.PLANE_POINT, "offset" : 25 * mm, "width" : 150 * mm, "height" : 150 * mm});
        }
        {
            var Q0;
            Q0=makeQuery(id+"F7.opRevolve","SWEPT_BODY",BODY,{"disambiguationData":[OSD([sQuery(id+"F2.wireOp",EDGE,"E0.bottom"),sQuery(id+"F2.wireOp",EDGE,"E0.top"),sQuery(id+"F2.wireOp",EDGE,"E0.left"),sQuery(id+"F2.wireOp",EDGE,"E0.right"),sQuery(id+"F2.wireOp",EDGE,"E9")])]});
            var Q1;
            Q1=qCreatedBy(id+"F21.planeOp",FACE);
            mirror(context, id + "F22", {"entities" : qUnion([Q0]), "mirrorPlane" : qUnion([Q1])});
        }
        {
            var Q0;
            Q0=makeQuery(id+"F17.opPattern","COPY",FACE,{"derivedFrom":makeQuery(id+"F4.opRevolve","SWEPT_FACE",FACE,{"disambiguationData":[OSD([sQuery(id+"F2.wireOp",EDGE,"E3")])]}),"instanceName":"1"});
            var sketch = newSketch(context, id + "F23", { "sketchPlane" : qUnion([Q0])});
            skLineSegment(sketch, "E199", {"start": v(-196.98, 277.5) * mm, "end": v(-238.1, 233.81) * mm});
            skLineSegment(sketch, "E200", {"start": v(-238.1, 233.81) * mm, "end": v(-236.74, 232.54) * mm});
            skLineSegment(sketch, "E201", {"start": v(-234.46, 230.39) * mm, "end": v(-178.74, 289.6) * mm});
            skArc(sketch, "E202.0", {"start": v(-178.74, 289.6) * mm, "mid": v(-187.96, 283.7) * mm, "end": v(-196.98, 277.5) * mm});
            skArc(sketch, "E203.0", {"start": v(-294.95, 206.95) * mm, "mid": v(-300.58, 198.68) * mm, "end": v(-305.98, 190.26) * mm});
            skLineSegment(sketch, "E204", {"start": v(-294.95, 206.95) * mm, "end": v(-278.58, 195.46) * mm});
            skLineSegment(sketch, "E205", {"start": v(-272.72, 203.56) * mm, "end": v(-263.1, 196.38) * mm});
            skArc(sketch, "E206.trimOffspring", {"start": v(-272.72, 203.56) * mm, "mid": v(-275.68, 199.53) * mm, "end": v(-278.58, 195.46) * mm});
            skPoint(sketch, "E207.orphan", {"position": v(-170.15, 294.72) * mm});
            skLineSegment(sketch, "E208", {"start": v(-289, 179.7) * mm, "end": v(-305.98, 190.26) * mm});
            skArc(sketch, "E209", {"start": v(-278.58, 195.46) * mm, "mid": v(-283.9, 187.65) * mm, "end": v(-289, 179.7) * mm});
            skArc(sketch, "E210", {"start": v(-289, 179.7) * mm, "mid": v(-291.9, 174.95) * mm, "end": v(-294.72, 170.15) * mm});
            skCircle(sketch, "E211", {"center": v(-288.07, 190.41) * mm, "radius": 1.5 * mm});
            skLineSegment(sketch, "E212", {"start": v(-300.58, 198.68) * mm, "end": v(-283.9, 187.65) * mm, "construction": true});
            skPoint(sketch, "E213", {"position": v(-294.32, 194.55) * mm});
            skLineSegment(sketch, "E214", {"start": v(-291.57, 198.72) * mm, "end": v(-297.08, 190.37) * mm, "construction": true});
            skLineSegment(sketch, "E215", {"start": v(-236.74, 232.54) * mm, "end": v(-243.6, 225.25) * mm});
            skLineSegment(sketch, "E216", {"start": v(-243.6, 225.25) * mm, "end": v(-242.67, 224.38) * mm});
            skLineSegment(sketch, "E217", {"start": v(-242.67, 224.38) * mm, "end": v(-235.82, 231.67) * mm});
            skLineSegment(sketch, "E218", {"start": v(-236.74, 232.54) * mm, "end": v(-235.82, 231.67) * mm});
            skLineSegment(sketch, "E219", {"start": v(-235.82, 231.67) * mm, "end": v(-234.46, 230.39) * mm});
            skLineSegment(sketch, "E220", {"start": v(-278.58, 195.46) * mm, "end": v(-268.76, 188.57) * mm, "construction": true});
            skLineSegment(sketch, "E221", {"start": v(-289, 179.7) * mm, "end": v(-278.8, 173.36) * mm, "construction": true});
            skPoint(sketch, "E222", {"position": v(-273.67, 192.01) * mm});
            skPoint(sketch, "E223", {"position": v(-283.9, 176.53) * mm});
            skSolve(sketch);
        }
        {
            var Q0;
            {var subQ0=sQuery(id+"F23.wireOp",EDGE,"E199");Q0=makeQuery(id+"F23.imprint","IMPRINT",FACE,{"disambiguationData":[TD([[makeQuery(id+"F23.imprint","IMPRINT",EDGE,{"derivedFrom":subQ0}),1.0]])]});}
            extrude(context, id + "F24", {"entities" : qUnion([Q0]), "operationType" : NewBodyOperationType.REMOVE, "oppositeDirection" : true, "depth" : 22 * mm / 2 + getVariable(context, 'depth') / 2, "hasSecondDirection" : true, "secondDirectionOppositeDirection" : false, "secondDirectionDepth" : 22 * mm / 2 - getVariable(context, 'depth') / 2});
        }
        {
            var Q0;
            Q0=makeQuery(id+"F23.imprint","IMPRINT",FACE,{"disambiguationData":[TD([[makeQuery(id+"F23.imprint","IMPRINT",EDGE,{"derivedFrom":sQuery(id+"F23.wireOp",EDGE,"E215")}),1.0]])]});
            extrude(context, id + "F25", {"entities" : qUnion([Q0]), "operationType" : NewBodyOperationType.REMOVE, "oppositeDirection" : true, "depth" : 10 * mm});
        }
        {
            var Q0;
            {var subQ10=sQuery(id+"F23.wireOp",EDGE,"E205");Q0=makeQuery(id+"F23.imprint","IMPRINT",FACE,{"disambiguationData":[TD([[makeQuery(id+"F23.imprint","IMPRINT",EDGE,{"derivedFrom":subQ10}),-1.0]])]});}
            extrude(context, id + "F26", {"entities" : qUnion([Q0]), "operationType" : NewBodyOperationType.REMOVE, "oppositeDirection" : true, "depth" : 1.5 * mm});
        }
        {
            var Q0;
            Q0=makeQuery(id+"F23.imprint","IMPRINT",FACE,{"disambiguationData":[TD([[makeQuery(id+"F23.imprint","IMPRINT",EDGE,{"derivedFrom":sQuery(id+"F23.wireOp",EDGE,"E203.0")}),1.0]])]});
            var Q1;
            {var subQ10=sQuery(id+"F23.wireOp",EDGE,"E205");Q1=makeQuery(id+"F23.imprint","IMPRINT",FACE,{"disambiguationData":[TD([[makeQuery(id+"F23.imprint","IMPRINT",EDGE,{"derivedFrom":subQ10}),-1.0]])]});}
            var Q2;
            Q2=makeQuery(id+"F26.boolean.opBoolean","COPY",FACE,{"derivedFrom":makeQuery(id+"F26.opExtrude","CAP_FACE",FACE,{"disambiguationData":[OSD([sQuery(id+"F2.wireOp",EDGE,"E3"),sQuery(id+"F8.wireOp",EDGE,"E19"),sQuery(id+"F8.wireOp",EDGE,"E20"),sQuery(id+"F8.wireOp",EDGE,"E22.MirrorCS"),sQuery(id+"F8.wireOp",EDGE,"E23.MirrorCS"),sQuery(id+"F14.wireOp",EDGE,"E29.bottom"),sQuery(id+"F14.wireOp",EDGE,"E29.right"),sQuery(id+"F23.wireOp",EDGE,"E205"),sQuery(id+"F23.wireOp",EDGE,"E206.trimOffspring"),sQuery(id+"F23.wireOp",EDGE,"E209"),sQuery(id+"F23.wireOp",EDGE,"E210")])],"isStart":false})});
            extrude(context, id + "F27", {"entities" : qUnion([Q0, Q1]), "endBound" : BoundingType.UP_TO_SURFACE, "oppositeDirection" : true, "endBoundEntityFace" : qUnion([Q2]), "depth" : 25 * mm});
        }
        {
            var Q0;
            Q0=sQuery(id+"F23.wireOp",VERTEX,"E214.start");
            var Q1;
            Q1=sQuery(id+"F23.wireOp",VERTEX,"E214.end");
            var Q2;
            Q2=sQuery(id+"F23.wireOp",VERTEX,"E223");
            var Q3;
            Q3=sQuery(id+"F23.wireOp",VERTEX,"E222");
            var Q4;
            Q4=makeQuery(id+"F27.opExtrude","SWEPT_BODY",BODY,{"disambiguationData":[OSD([sQuery(id+"F2.wireOp",EDGE,"E3"),sQuery(id+"F8.wireOp",EDGE,"E19"),sQuery(id+"F8.wireOp",EDGE,"E20"),sQuery(id+"F8.wireOp",EDGE,"E22.MirrorCS"),sQuery(id+"F8.wireOp",EDGE,"E23.MirrorCS"),sQuery(id+"F14.wireOp",EDGE,"E29.bottom"),sQuery(id+"F14.wireOp",EDGE,"E29.right"),sQuery(id+"F23.wireOp",EDGE,"E203.0"),sQuery(id+"F23.wireOp",EDGE,"E204"),sQuery(id+"F23.wireOp",EDGE,"E205"),sQuery(id+"F23.wireOp",EDGE,"E206.trimOffspring"),sQuery(id+"F23.wireOp",EDGE,"E208"),sQuery(id+"F23.wireOp",EDGE,"E210"),sQuery(id+"F23.wireOp",EDGE,"E211")])]});
            hole(context, id + "F28", {"style" : HoleStyle.SIMPLE, "endStyle" : HoleEndStyle.BLIND, "standardTappedOrClearance" : lookupTablePath({ "standard" : "ISO", "engagement" : "75%", "pitch" : "0.6 mm", "size" : "M3", "type" : "Tapped" }), "standardBlindInLast" : lookupTablePath({ "standard" : "ISO", "engagement" : "75%", "pitch" : "0.6 mm", "size" : "M3", "type" : "Tapped" }), "holeDiameter" : 2.4 * mm, "holeDepth" : 6.35 * mm, "locations" : qUnion([Q0, Q1, Q2, Q3]), "scope" : qUnion([Q4])});
        }
        {
            var Q0;
            Q0=makeQuery(id+"F27.opExtrude","SWEPT_EDGE",EDGE,{"disambiguationData":[OSD([sQuery(id+"F23.wireOp",EDGE,"E204"),sQuery(id+"F23.wireOp",EDGE,"E206.trimOffspring"),sQuery(id+"F23.wireOp",EDGE,"E209")])]});
            var Q1;
            Q1=makeQuery(id+"F27.opExtrude","SWEPT_EDGE",EDGE,{"disambiguationData":[OSD([sQuery(id+"F23.wireOp",EDGE,"E203.0"),sQuery(id+"F23.wireOp",EDGE,"E204")])]});
            var Q2;
            Q2=makeQuery(id+"F27.opExtrude","SWEPT_EDGE",EDGE,{"disambiguationData":[OSD([sQuery(id+"F23.wireOp",EDGE,"E203.0"),sQuery(id+"F23.wireOp",EDGE,"E208")])]});
            var Q3;
            Q3=makeQuery(id+"F27.opExtrude","SWEPT_EDGE",EDGE,{"disambiguationData":[OSD([sQuery(id+"F23.wireOp",EDGE,"E208"),sQuery(id+"F23.wireOp",EDGE,"E209"),sQuery(id+"F23.wireOp",EDGE,"E210")])]});
            var Q4;
            Q4=makeQuery(id+"FnrsBtJmM2bQirG_17.1.F27.opExtrude","SWEPT_EDGE",EDGE,{"disambiguationData":[OSD([sQuery(id+"F23.wireOp",EDGE,"E204"),sQuery(id+"F23.wireOp",EDGE,"E206.trimOffspring"),sQuery(id+"F23.wireOp",EDGE,"E209")])]});
            var Q5;
            Q5=makeQuery(id+"FnrsBtJmM2bQirG_17.1.F27.opExtrude","SWEPT_EDGE",EDGE,{"disambiguationData":[OSD([sQuery(id+"F23.wireOp",EDGE,"E203.0"),sQuery(id+"F23.wireOp",EDGE,"E204")])]});
            var Q6;
            Q6=makeQuery(id+"FnrsBtJmM2bQirG_17.1.F27.opExtrude","SWEPT_EDGE",EDGE,{"disambiguationData":[OSD([sQuery(id+"F23.wireOp",EDGE,"E208"),sQuery(id+"F23.wireOp",EDGE,"E209"),sQuery(id+"F23.wireOp",EDGE,"E210")])]});
            var Q7;
            Q7=makeQuery(id+"FnrsBtJmM2bQirG_17.1.F27.opExtrude","SWEPT_EDGE",EDGE,{"disambiguationData":[OSD([sQuery(id+"F23.wireOp",EDGE,"E203.0"),sQuery(id+"F23.wireOp",EDGE,"E208")])]});
            fillet(context, id + "F29", {"entities" : qUnion([Q0, Q1, Q2, Q3, Q4, Q5, Q6, Q7]), "radius" : 5 * mm, "tangentPropagation" : true, "allowEdgeOverflow" : false});
        }
        {
            var Q0;
            Q0=makeQuery(id+"F17.opPattern","COPY",FACE,{"derivedFrom":makeQuery(id+"F4.opRevolve","SWEPT_FACE",FACE,{"disambiguationData":[OSD([sQuery(id+"F2.wireOp",EDGE,"E3")])]}),"instanceName":"4"});
            var sketch = newSketch(context, id + "F30", { "sketchPlane" : qUnion([Q0])});
            skText(sketch, "E224", { "text": "who/tommie 2016", "fontName": "OpenSans-Bold.ttf"});
            skLineSegment(sketch, "E225", {"start": v(223.42, 251.37) * mm, "end": v(226.08, 254.36) * mm, "construction": true});
            skLineSegment(sketch, "E226", {"start": v(219.43, 246.89) * mm, "end": v(218.1, 245.4) * mm, "construction": true});
            const initialGuessF30  = {"E224": [0.1913, 0.2719, 0.74744, -0.66433, 0.006]};
            skSetInitialGuess(sketch, initialGuessF30);
            skSolve(sketch);
        }
        {
            var Q0;
            Q0 = qSketchRegion(id + "F30", true);
            extrude(context, id + "F31", {"entities" : qUnion([Q0]), "operationType" : NewBodyOperationType.REMOVE, "oppositeDirection" : true, "depth" : 1 * mm, "hasDraft" : true, "draftAngle" : 3 * degree});
        }
    });
